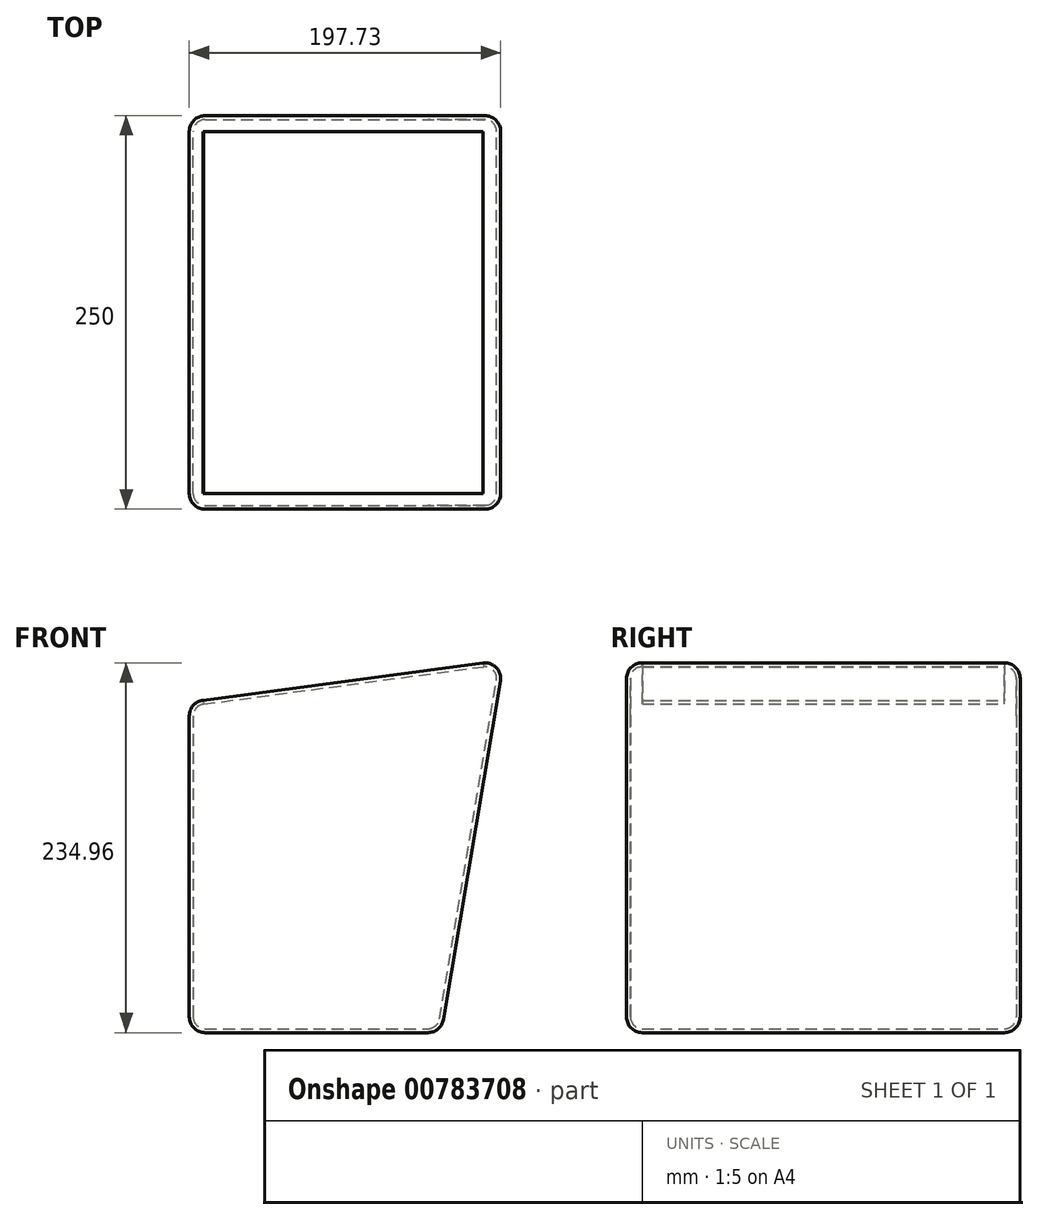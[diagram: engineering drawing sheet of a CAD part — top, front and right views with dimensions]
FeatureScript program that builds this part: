
annotation { "Feature Type Name" : "Feature", "Feature Type Description" : "" }
export const myFeature = defineFeature(function(context is Context, id is Id, definition is map)
    precondition{}
    {
        {
            var Q0;
            Q0=qCreatedBy(makeId("Front.planeOp"),FACE);
            var sketch = newSketch(context, id + "F0", { "sketchPlane" : qUnion([Q0])});
            skLineSegment(sketch, "E0", {"start": v(6.2, 35.42) * mm, "end": v(6.2, -174.58) * mm});
            skLineSegment(sketch, "E1", {"start": v(6.2, -174.58) * mm, "end": v(166.2, -174.58) * mm});
            skLineSegment(sketch, "E2", {"start": v(166.2, -174.58) * mm, "end": v(206.04, 62.09) * mm});
            skLineSegment(sketch, "E3", {"start": v(206.04, 62.09) * mm, "end": v(6.2, 35.42) * mm});
            skSolve(sketch);
        }
        {
            var Q0;
            Q0=makeQuery(id+"F0.imprint","IMPRINT",FACE,{"disambiguationData":[TD([[makeQuery(id+"F0.imprint","IMPRINT",EDGE,{"derivedFrom":sQuery(id+"F0.wireOp",EDGE,"E0")}),1.0]])]});
            extrude(context, id + "F1", {"entities" : qUnion([Q0]), "depth" : 125 * mm, "offsetDistance" : 25 * mm});
        }
        {
            var Q0;
            Q0=makeQuery(id+"F1.opExtrude","SWEPT_BODY",BODY,{"disambiguationData":[OSD([sQuery(id+"F0.wireOp",EDGE,"E0"),sQuery(id+"F0.wireOp",EDGE,"E1"),sQuery(id+"F0.wireOp",EDGE,"E2"),sQuery(id+"F0.wireOp",EDGE,"E3")])]});
            var Q1;
            Q1=qCreatedBy(makeId("Front.planeOp"),FACE);
            mirror(context, id + "F2", {"operationType" : NewBodyOperationType.ADD, "entities" : qUnion([Q0]), "mirrorPlane" : qUnion([Q1])});
        }
        {
            var Q0;
            Q0=makeQuery(id+"F1.opExtrude","CAP_EDGE",EDGE,{"disambiguationData":[OSD([sQuery(id+"F0.wireOp",EDGE,"E3")])],"isStart":false});
            var Q1;
            {var subQ0=makeQuery(id+"F1.opExtrude","SWEPT_EDGE",EDGE,{"disambiguationData":[OSD([sQuery(id+"F0.wireOp",EDGE,"E2"),sQuery(id+"F0.wireOp",EDGE,"E3")])]});Q1=makeQuery(id+"F2.boolean.opBoolean","MERGE",EDGE,{"derivedFrom":[subQ0,makeQuery(id+"F2.opPattern","COPY",EDGE,{"derivedFrom":subQ0,"instanceName":"1"})]});}
            var Q2;
            Q2=makeQuery(id+"F1.opExtrude","CAP_EDGE",EDGE,{"disambiguationData":[OSD([sQuery(id+"F0.wireOp",EDGE,"E2")])],"isStart":false});
            var Q3;
            Q3=makeQuery(id+"F1.opExtrude","CAP_EDGE",EDGE,{"disambiguationData":[OSD([sQuery(id+"F0.wireOp",EDGE,"E0")])],"isStart":false});
            var Q4;
            Q4=makeQuery(id+"F1.opExtrude","CAP_EDGE",EDGE,{"disambiguationData":[OSD([sQuery(id+"F0.wireOp",EDGE,"E1")])],"isStart":false});
            var Q5;
            {var subQ0=makeQuery(id+"F1.opExtrude","SWEPT_EDGE",EDGE,{"disambiguationData":[OSD([sQuery(id+"F0.wireOp",EDGE,"E1"),sQuery(id+"F0.wireOp",EDGE,"E2")])]});Q5=makeQuery(id+"F2.boolean.opBoolean","MERGE",EDGE,{"derivedFrom":[subQ0,makeQuery(id+"F2.opPattern","COPY",EDGE,{"derivedFrom":subQ0,"instanceName":"1"})]});}
            var Q6;
            Q6=makeQuery(id+"F2.opPattern","COPY",EDGE,{"derivedFrom":makeQuery(id+"F1.opExtrude","CAP_EDGE",EDGE,{"disambiguationData":[OSD([sQuery(id+"F0.wireOp",EDGE,"E3")])],"isStart":false}),"instanceName":"1"});
            var Q7;
            {var subQ0=makeQuery(id+"F1.opExtrude","SWEPT_EDGE",EDGE,{"disambiguationData":[OSD([sQuery(id+"F0.wireOp",EDGE,"E0"),sQuery(id+"F0.wireOp",EDGE,"E3")])]});Q7=makeQuery(id+"F2.boolean.opBoolean","MERGE",EDGE,{"derivedFrom":[subQ0,makeQuery(id+"F2.opPattern","COPY",EDGE,{"derivedFrom":subQ0,"instanceName":"1"})]});}
            var Q8;
            Q8=makeQuery(id+"F2.opPattern","COPY",EDGE,{"derivedFrom":makeQuery(id+"F1.opExtrude","CAP_EDGE",EDGE,{"disambiguationData":[OSD([sQuery(id+"F0.wireOp",EDGE,"E2")])],"isStart":false}),"instanceName":"1"});
            var Q9;
            Q9=makeQuery(id+"F2.opPattern","COPY",EDGE,{"derivedFrom":makeQuery(id+"F1.opExtrude","CAP_EDGE",EDGE,{"disambiguationData":[OSD([sQuery(id+"F0.wireOp",EDGE,"E0")])],"isStart":false}),"instanceName":"1"});
            var Q10;
            Q10=makeQuery(id+"F2.opPattern","COPY",EDGE,{"derivedFrom":makeQuery(id+"F1.opExtrude","CAP_EDGE",EDGE,{"disambiguationData":[OSD([sQuery(id+"F0.wireOp",EDGE,"E1")])],"isStart":false}),"instanceName":"1"});
            var Q11;
            {var subQ0=makeQuery(id+"F1.opExtrude","SWEPT_EDGE",EDGE,{"disambiguationData":[OSD([sQuery(id+"F0.wireOp",EDGE,"E0"),sQuery(id+"F0.wireOp",EDGE,"E1")])]});Q11=makeQuery(id+"F2.boolean.opBoolean","MERGE",EDGE,{"derivedFrom":[subQ0,makeQuery(id+"F2.opPattern","COPY",EDGE,{"derivedFrom":subQ0,"instanceName":"1"})]});}
            fillet(context, id + "F3", {"entities" : qUnion([Q0, Q1, Q2, Q3, Q4, Q5, Q6, Q7, Q8, Q9, Q10, Q11]), "radius" : 10 * mm, "tangentPropagation" : true, "allowEdgeOverflow" : false});
        }
        {
            var Q0;
            {var subQ0=makeQuery(id+"F1.opExtrude","SWEPT_FACE",FACE,{"disambiguationData":[OSD([sQuery(id+"F0.wireOp",EDGE,"E3")])]});Q0=makeQuery(id+"F2.boolean.opBoolean","MERGE",FACE,{"derivedFrom":[subQ0,makeQuery(id+"F2.opPattern","COPY",FACE,{"derivedFrom":subQ0,"instanceName":"1"})]});}
            shell(context, id + "F4", {"entities" : qUnion([Q0]), "thickness" : 2.5 * mm});
        }
    });
